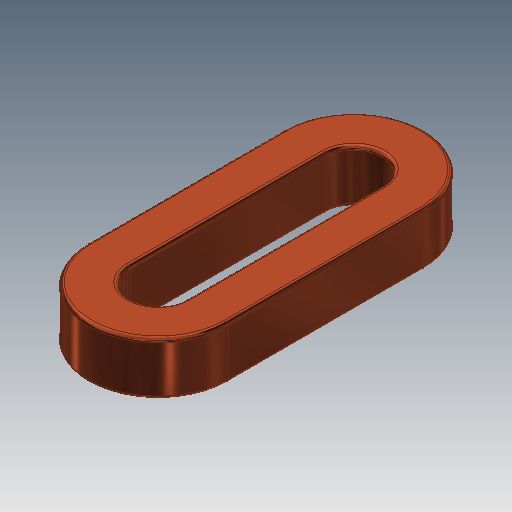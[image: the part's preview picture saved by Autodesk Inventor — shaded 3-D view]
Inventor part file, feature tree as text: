
AUTODESK INVENTOR PART (.ipt)
format: ipt  version: 2020.2 (Build 242310000, 310)  size: 161,280 bytes
history: native  units: mm
features: extrude x1, fillet x1, sketch x1
ambient origin geometry x8: Origin, YZ Plane, XZ Plane, XY Plane, X Axis, Y Axis, Z Axis, Center Point
bodies: Body1 (feature_tree)
feature tree (3):
  extrude  "Extrusion7"  Depth=10.0mm
  fillet  "Fillet8"  Radius=3.0mm
  sketch  "Sketch11"  dims[d82=14.0mm d83=10.0mm d84=3.0mm d85=3.8mm d86=0.0mm d87=0.25mm]
